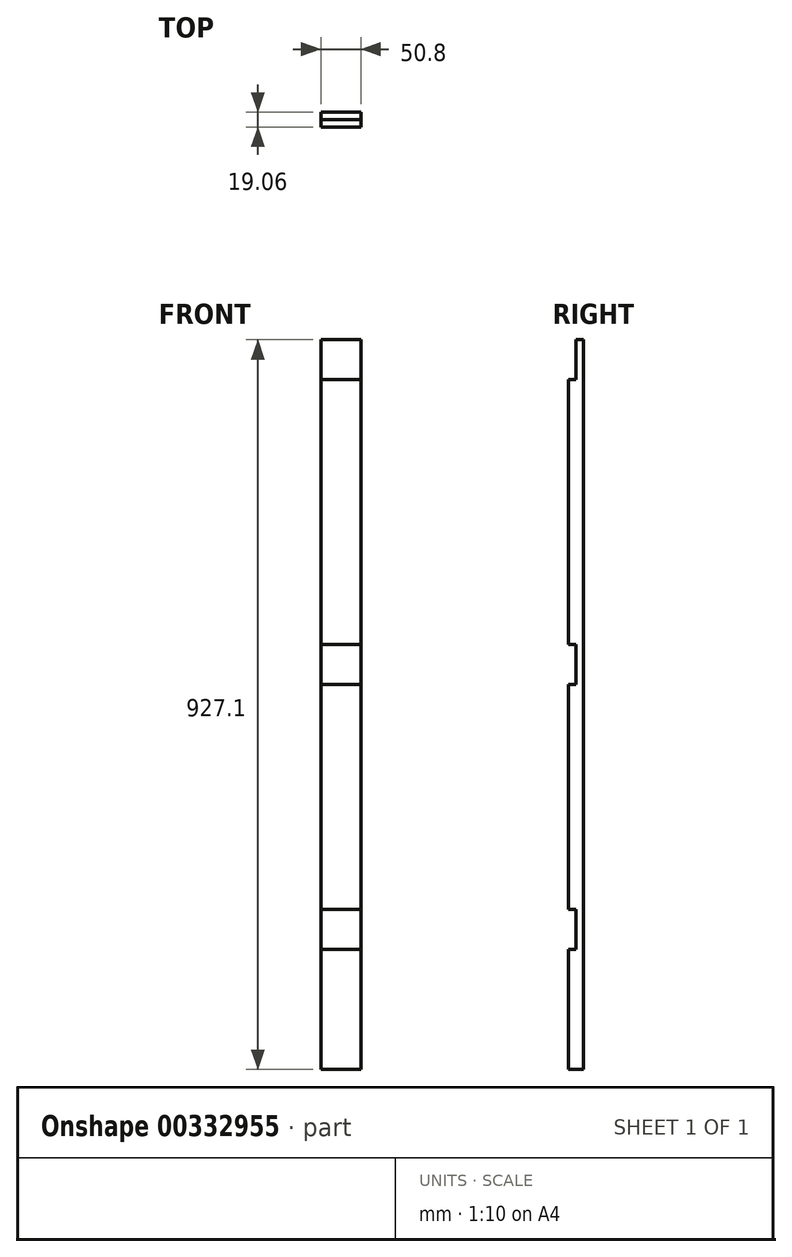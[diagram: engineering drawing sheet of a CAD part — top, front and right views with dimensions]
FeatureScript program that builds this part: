
annotation { "Feature Type Name" : "Feature", "Feature Type Description" : "" }
export const myFeature = defineFeature(function(context is Context, id is Id, definition is map)
    precondition{}
    {
        {
            var Q0;
            Q0=qCreatedBy(makeId("Top.planeOp"),FACE);
            var sketch = newSketch(context, id + "F0", { "sketchPlane" : qUnion([Q0])});
            skLineSegment(sketch, "E0.bottom", {"start": v(25.4, 9.53) * mm, "end": v(-25.4, 9.53) * mm});
            skLineSegment(sketch, "E0.top", {"start": v(25.4, -9.53) * mm, "end": v(-25.4, -9.53) * mm});
            skLineSegment(sketch, "E0.left", {"start": v(25.4, 9.53) * mm, "end": v(25.4, -9.52) * mm});
            skLineSegment(sketch, "E0.right", {"start": v(-25.4, 9.53) * mm, "end": v(-25.4, -9.53) * mm});
            skPoint(sketch, "E0.middle", {"position": v(0, 0) * mm});
            skSolve(sketch);
        }
        {
            var Q0;
            Q0=makeQuery(id+"F0.imprint","IMPRINT",FACE,{"disambiguationData":[TD([[makeQuery(id+"F0.imprint","IMPRINT",EDGE,{"derivedFrom":sQuery(id+"F0.wireOp",EDGE,"E0.bottom")}),1.0]])]});
            var Q1;
            Q1=qSketchRegion(id+"F2",true);
            extrude(context, id + "F1", {"entities" : qUnion([Q0, Q1]), "depth" : 927.1 * mm});
        }
        {
            var Q0;
            Q0=qCreatedBy(makeId("Front.planeOp"),FACE);
            var sketch = newSketch(context, id + "F2", { "sketchPlane" : qUnion([Q0])});
            skLineSegment(sketch, "E1.bottom", {"start": v(-38.77, 152.4) * mm, "end": v(83.66, 152.4) * mm});
            skLineSegment(sketch, "E1.top", {"start": v(-38.77, 203.2) * mm, "end": v(83.66, 203.2) * mm});
            skLineSegment(sketch, "E1.left", {"start": v(-38.77, 152.4) * mm, "end": v(-38.77, 203.2) * mm});
            skLineSegment(sketch, "E1.right", {"start": v(83.66, 152.4) * mm, "end": v(83.66, 203.2) * mm});
            skLineSegment(sketch, "E2.bottom", {"start": v(-210.36, 876.3) * mm, "end": v(132.8, 876.3) * mm});
            skLineSegment(sketch, "E2.top", {"start": v(-210.36, 927.1) * mm, "end": v(132.8, 927.1) * mm});
            skLineSegment(sketch, "E2.left", {"start": v(-210.36, 876.3) * mm, "end": v(-210.36, 927.1) * mm});
            skLineSegment(sketch, "E2.right", {"start": v(132.8, 876.3) * mm, "end": v(132.8, 927.1) * mm});
            skLineSegment(sketch, "E3.bottom", {"start": v(-114.6, 539.75) * mm, "end": v(66.62, 539.75) * mm});
            skLineSegment(sketch, "E3.top", {"start": v(-114.6, 488.95) * mm, "end": v(66.62, 488.95) * mm});
            skLineSegment(sketch, "E3.left", {"start": v(-114.6, 539.75) * mm, "end": v(-114.6, 488.95) * mm});
            skLineSegment(sketch, "E3.right", {"start": v(66.62, 539.75) * mm, "end": v(66.62, 488.95) * mm});
            skSolve(sketch);
        }
        {
            var Q0;
            Q0=qSketchRegion(id+"F2",true);
            extrude(context, id + "F3", {"entities" : qUnion([Q0]), "operationType" : NewBodyOperationType.REMOVE, "depth" : 25.4 * mm});
        }
    });
